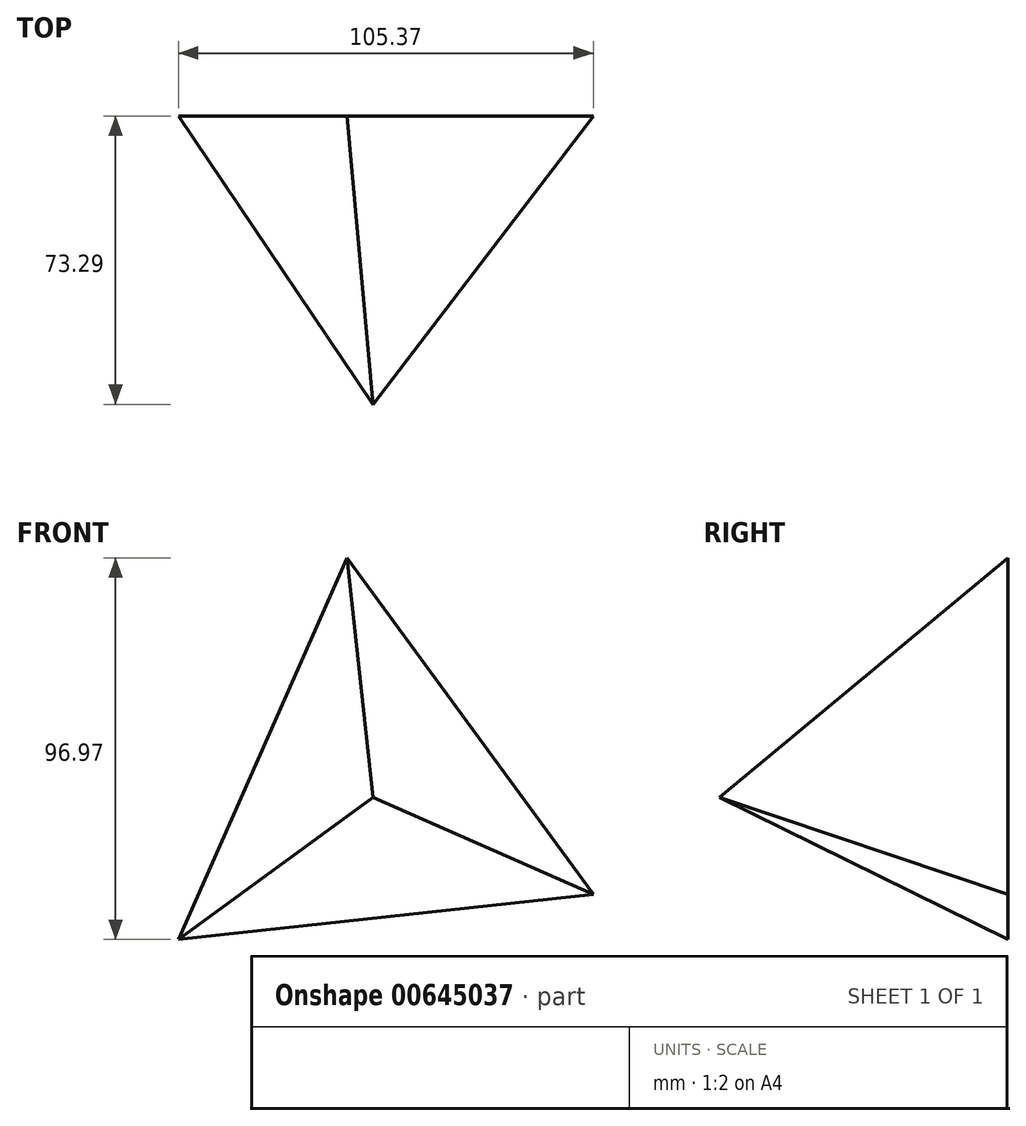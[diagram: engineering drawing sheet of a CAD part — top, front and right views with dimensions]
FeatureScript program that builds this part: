
annotation { "Feature Type Name" : "Feature", "Feature Type Description" : "" }
export const myFeature = defineFeature(function(context is Context, id is Id, definition is map)
    precondition{}
    {
        {
            var Q0;
            Q0=qCreatedBy(makeId("Front.planeOp"),FACE);
            var sketch = newSketch(context, id + "F0", { "sketchPlane" : qUnion([Q0])});
            skCircle(sketch, "E0.cCircle", {"center": v(0, 0) * mm, "radius": 30.6 * mm, "construction": true});
            skLineSegment(sketch, "E0.0", {"start": v(-6.6, 60.84) * mm, "end": v(55.98, -24.71) * mm});
            skLineSegment(sketch, "E0.1", {"start": v(55.98, -24.71) * mm, "end": v(-49.4, -36.13) * mm});
            skLineSegment(sketch, "E0.2", {"start": v(-49.4, -36.13) * mm, "end": v(-6.6, 60.84) * mm});
            skPoint(sketch, "E0.0.midPoint", {"position": v(24.7, 18.06) * mm});
            skSolve(sketch);
        }
        {
            var Q0;
            Q0=qCreatedBy(makeId("Right.planeOp"),FACE);
            var sketch = newSketch(context, id + "F1", { "sketchPlane" : qUnion([Q0])});
            skPoint(sketch, "E1", {"position": v(-73.3, 0) * mm});
            skSolve(sketch);
        }
        {
            var Q0;
            Q0 = qSketchRegion(id + "F0", true);
            var Q1;
            Q1=sQuery(id+"F1.wireOp",VERTEX,"E1");
            loft(context, id + "F2", {"sheetProfilesArray" : [{ "sheetProfileEntities" : qUnion([Q0]) }, { "sheetProfileEntities" : qUnion([Q1]) }]});
        }
    });
